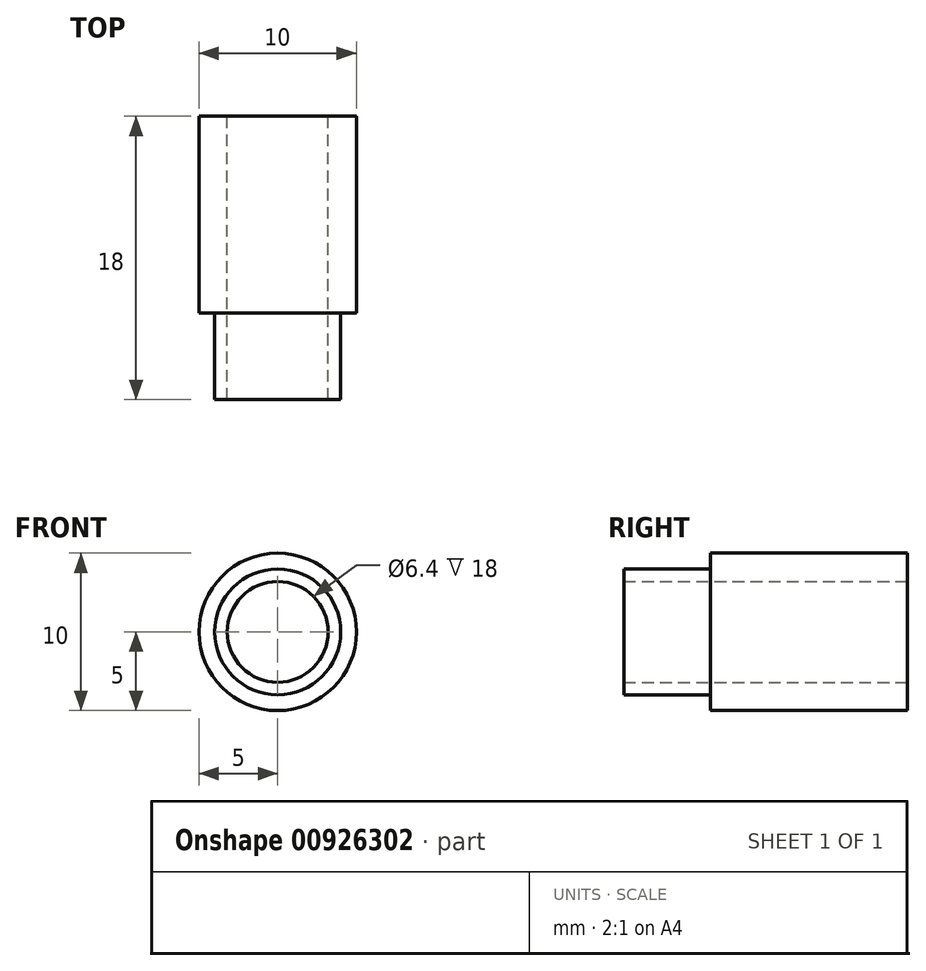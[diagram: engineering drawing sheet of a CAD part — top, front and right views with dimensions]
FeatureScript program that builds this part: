
annotation { "Feature Type Name" : "Feature", "Feature Type Description" : "" }
export const myFeature = defineFeature(function(context is Context, id is Id, definition is map)
    precondition{}
    {
        {
            var Q0;
            Q0=qCreatedBy(makeId("Front.planeOp"),FACE);
            var sketch = newSketch(context, id + "F0", { "sketchPlane" : qUnion([Q0])});
            skCircle(sketch, "E0", {"center": v(0, 0) * mm, "radius": 5 * mm});
            skSolve(sketch);
        }
        {
            var Q0;
            Q0 = qSketchRegion(id + "F0", true);
            extrude(context, id + "F1", {"entities" : qUnion([Q0]), "depth" : 12.5 * mm, "offsetDistance" : 25 * mm});
        }
        {
            var Q0;
            Q0=makeQuery(id+"F1.opExtrude","CAP_FACE",FACE,{"disambiguationData":[OSD([sQuery(id+"F0.wireOp",EDGE,"E0")])],"isStart":false});
            var sketch = newSketch(context, id + "F2", { "sketchPlane" : qUnion([Q0])});
            skCircle(sketch, "E1", {"center": v(0, 0) * mm, "radius": 4 * mm});
            skSolve(sketch);
        }
        {
            var Q0;
            Q0=makeQuery(id+"F2.imprint","IMPRINT",FACE,{"disambiguationData":[TD([[makeQuery(id+"F2.imprint","IMPRINT",EDGE,{"derivedFrom":sQuery(id+"F2.wireOp",EDGE,"E1")}),1.0]])]});
            extrude(context, id + "F3", {"entities" : qUnion([Q0]), "operationType" : NewBodyOperationType.ADD, "depth" : 5.5 * mm, "offsetDistance" : 25 * mm});
        }
        {
            var Q0;
            Q0=makeQuery(id+"F1.opExtrude","CAP_FACE",FACE,{"disambiguationData":[OSD([sQuery(id+"F0.wireOp",EDGE,"E0")])],"isStart":true});
            var sketch = newSketch(context, id + "F4", { "sketchPlane" : qUnion([Q0])});
            skPoint(sketch, "E2", {"position": v(0, 0) * mm});
            skSolve(sketch);
        }
        {
            var Q0;
            Q0=sQuery(id+"F4.wireOp",VERTEX,"E2");
            var Q1;
            Q1=makeQuery(id+"F1.opExtrude","SWEPT_BODY",BODY,{"disambiguationData":[OSD([sQuery(id+"F0.wireOp",EDGE,"E0")])]});
            hole(context, id + "F5", {"style" : HoleStyle.SIMPLE, "endStyle" : HoleEndStyle.THROUGH, "standardTappedOrClearance" : lookupTablePath({ "standard" : "ISO", "size" : "6.4", "type" : "Drilled" }), "standardBlindInLast" : lookupTablePath({ "standard" : "ISO", "size" : "6.4", "type" : "Drilled" }), "holeDiameter" : 6.4 * mm, "majorDiameter" : 5 * mm, "isTappedThrough" : true, "tappedDepth" : 11.5 * mm, "tapClearance" : 3, "startFromSketch" : true, "locations" : qUnion([Q0]), "scope" : qUnion([Q1])});
        }
    });
